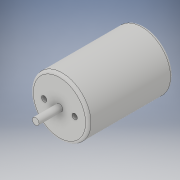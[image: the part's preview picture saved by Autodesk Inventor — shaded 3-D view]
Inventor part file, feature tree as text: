
AUTODESK INVENTOR PART (.ipt)
format: ipt  version: 2018 (Build 220112000, 112)  size: 124,928 bytes
history: native  units: in
note: dims shown in document units (in); Inventor stores cm internally (conversion verified against a paired STEP export)
features: extrude x3, sketch x1, fillet x1
ambient origin geometry x8: Origin, YZ Plane, XZ Plane, XY Plane, X Axis, Y Axis, Z Axis, Center Point
bodies: Solid1 (feature_tree)
feature tree (5):
  sketch  "Sketch1"  dims[d0=2.6772in d1=0.315in d2=0.7087in d3=0.7087in d4=0.25in d5=3.937in d6=0.0in d7=1.0in d8=0.0in d9=1.1024in d10=0.0in d11=0.125in]
  extrude  "Extrusion1"  Depth=0.125in
  extrude  "Extrusion2"  Depth=0.7087in
  extrude  "Extrusion3"  Depth=0.7087in
  fillet  "Fillet1"  Radius=0.25in
